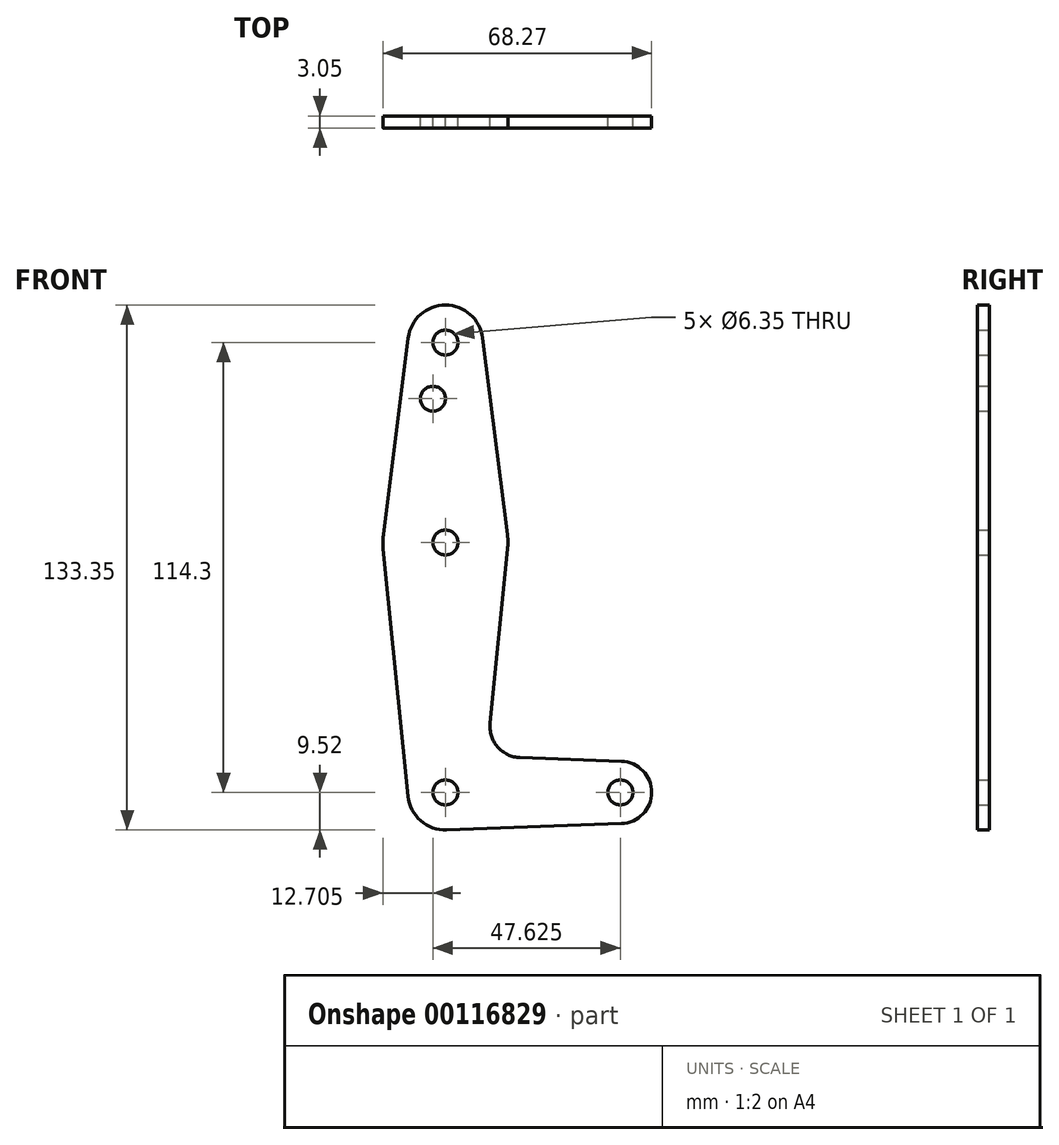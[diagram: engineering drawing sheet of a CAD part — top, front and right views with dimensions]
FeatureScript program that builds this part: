
annotation { "Feature Type Name" : "Feature", "Feature Type Description" : "" }
export const myFeature = defineFeature(function(context is Context, id is Id, definition is map)
    precondition{}
    {
        {
            var Q0;
            Q0=qCreatedBy(makeId("Front.planeOp"),FACE);
            var sketch = newSketch(context, id + "F0", { "sketchPlane" : qUnion([Q0])});
            skLineSegment(sketch, "E0", {"start": v(0, 0) * mm, "end": v(44.45, 0) * mm, "construction": true});
            skLineSegment(sketch, "E1", {"start": v(0, 0) * mm, "end": v(0, 63.5) * mm, "construction": true});
            skLineSegment(sketch, "E2", {"start": v(0, 63.5) * mm, "end": v(0, 114.3) * mm, "construction": true});
            skCircle(sketch, "E3", {"center": v(0, 0) * mm, "radius": 9.53 * mm});
            skCircle(sketch, "E4", {"center": v(44.45, 0) * mm, "radius": 7.94 * mm});
            skCircle(sketch, "E5", {"center": v(0, 63.5) * mm, "radius": 15.88 * mm});
            skCircle(sketch, "E6", {"center": v(0, 114.3) * mm, "radius": 9.53 * mm});
            skLineSegment(sketch, "E7", {"start": v(-9.48, -0.95) * mm, "end": v(-15.8, 61.91) * mm});
            skLineSegment(sketch, "E8", {"start": v(15.8, 61.91) * mm, "end": v(11.34, 17.6) * mm});
            skLineSegment(sketch, "E9", {"start": v(18.97, 8.85) * mm, "end": v(44.73, 7.93) * mm});
            skLineSegment(sketch, "E10", {"start": v(0.34, -9.52) * mm, "end": v(44.73, -7.93) * mm});
            skLineSegment(sketch, "E11", {"start": v(-15.75, 65.48) * mm, "end": v(-9.45, 115.5) * mm});
            skLineSegment(sketch, "E12", {"start": v(15.75, 65.48) * mm, "end": v(9.45, 115.5) * mm});
            skCircle(sketch, "E13", {"center": v(0, 114.3) * mm, "radius": 3.18 * mm});
            skCircle(sketch, "E14", {"center": v(0, 63.5) * mm, "radius": 3.18 * mm});
            skCircle(sketch, "E15", {"center": v(0, 0) * mm, "radius": 3.18 * mm});
            skCircle(sketch, "E16", {"center": v(44.45, 0) * mm, "radius": 3.18 * mm});
            skCircle(sketch, "E17", {"center": v(-3.18, 100.03) * mm, "radius": 3.18 * mm});
            skArc(sketch, "E18.filletArc", {"start": v(11.34, 17.6) * mm, "mid": v(13.26, 11.57) * mm, "end": v(18.97, 8.85) * mm});
            skSolve(sketch);
        }
        {
            var Q0;
            Q0 = qSketchRegion(id + "F0", true);
            extrude(context, id + "F1", {"entities" : qUnion([Q0]), "depth" : 3.05 * mm});
        }
    });
